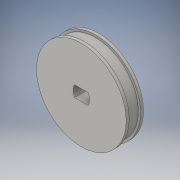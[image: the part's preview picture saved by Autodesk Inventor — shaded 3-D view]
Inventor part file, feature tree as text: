
AUTODESK INVENTOR PART (.ipt)
format: ipt  version: 2016 (Build 200138000, 138)  size: 129,024 bytes
history: native  units: in
note: dims shown in document units (in); Inventor stores cm internally (conversion verified against a paired STEP export)
features: extrude x4, sketch x3
ambient origin geometry x8: Origin, YZ Plane, XZ Plane, XY Plane, X Axis, Y Axis, Z Axis, Center Point
bodies: Body1 (feature_tree)
feature tree (7):
  extrude  "Extrusion3"  Depth=0.19in TaperAngle=0.0deg
  extrude  "Extrusion4"  Depth=0.05in TaperAngle=0.0deg
  extrude  "Extrusion5"  Depth=0.183in
  extrude  "Extrusion7"  Depth=0.186in
  sketch  "Sketch1"  dims[d0=1.427in d6=0.19in d7=0.0in]
  sketch  "Sketch4"  dims[d8=0.05in d9=0.0in d10=0.05in d11=0.0in]
  sketch  "Sketch5"  dims[d17=1.5in d18=1.5in d23=0.186in d24=0.183in d25=0.183in d26=0.277in d27=1.0in d28=0.0in]
